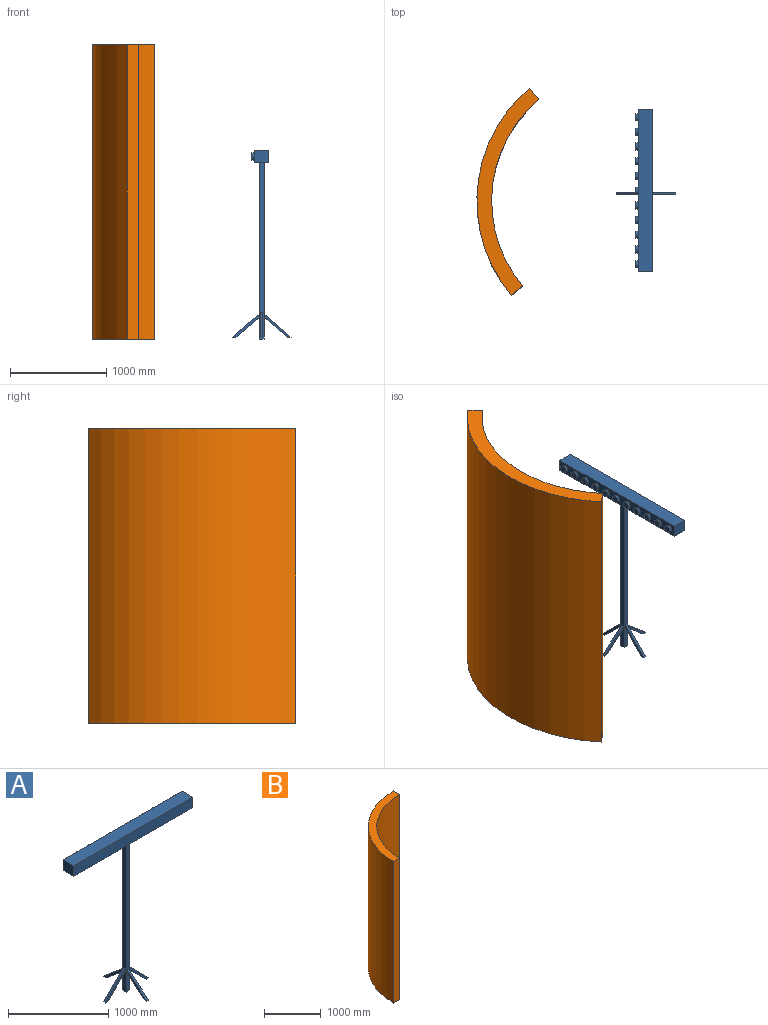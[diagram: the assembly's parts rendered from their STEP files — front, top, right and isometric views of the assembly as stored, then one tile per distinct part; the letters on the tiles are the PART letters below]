
ASSEMBLY  parts=2 mates=1
PART A: 53 faces, bbox 1676.4x609.6x1955.8 mm
  f0: plane 1828.8x50.8mm, normal (1,0,0), area 91990.6mm2, adj f2,f3,f4,f5,f16,f17,f18,f19
  f1: plane 1828.8x50.8mm, normal (-1,0,0), area 91990.6mm2, adj f2,f3,f4,f5,f12,f13,f14,f15
  f2: plane 50.8x50.8mm, normal (0,0,-1), area 2580.6mm2, adj f0,f1,f3,f4
  f3: plane 1828.8x50.8mm, normal (0,-1,0), area 92056.4mm2, adj f0,f1,f2,f5,f26,f28,f29,f30
  f4: plane 1828.8x50.8mm, normal (0,1,0), area 92056.4mm2, adj f0,f1,f2,f5,f22,f23,f24,f25
  f5: plane 1676.4x152.4mm, normal (0,0,-1), area 252902.7mm2, adj f0,f1,f3,f4,f6,f8,f9,f10
  f6: plane 152.4x127mm, normal (1,0,0), area 19354.8mm2, adj f5,f7,f9,f10
  f7: plane 1676.4x152.4mm, normal (0,0,1), area 255483.4mm2, adj f6,f8,f9,f10
  f8: plane 152.4x127mm, normal (-1,0,0), area 19354.8mm2, adj f5,f7,f9,f10
  f9: plane 1676.4x127mm, normal (0,-1,0), area 212902.8mm2, adj f5,f6,f7,f8
  f10: plane 1676.4x127mm, normal (0,1,0), area 162738.8mm2, adj f5,f6,f7,f8,f31,f33,f35,f37
  f11: plane 35.92x25.4mm, normal (0,0,-1), area 912.4mm2, adj f12,f13,f14,f15
  f12: plane 279.4x279.4mm, normal (0,-1,0), area 9391.2mm2, adj f1,f11,f14,f15
  f13: plane 279.4x279.4mm, normal (0,1,0), area 9391.2mm2, adj f1,f11,f14,f15
  f14: plane 243.48x243.48mm, normal (0.71,0,-0.71), area 8746mm2, adj f1,f11,f12,f13
  f15: plane 279.4x279.4mm, normal (-0.71,0,0.71), area 10036.3mm2, adj f1,f11,f12,f13
  f16: plane 243.48x243.48mm, normal (-0.71,0,-0.71), area 8746mm2, adj f0,f18,f19,f20
  f17: plane 279.4x279.4mm, normal (0.71,0,0.71), area 10036.3mm2, adj f0,f18,f19,f20
  f18: plane 279.4x279.4mm, normal (0,-1,0), area 9391.2mm2, adj f0,f16,f17,f20
  f19: plane 279.4x279.4mm, normal (0,1,0), area 9391.2mm2, adj f0,f16,f17,f20
  f20: plane 35.92x25.4mm, normal (0,0,-1), area 912.4mm2, adj f16,f17,f18,f19
  f21: plane 39.22x25.4mm, normal (0,0,-1), area 996.2mm2, adj f22,f23,f24,f25
  f22: plane 279.4x237.46mm, normal (-1,0,0), area 8659.9mm2, adj f4,f21,f24,f25
  f23: plane 279.4x237.46mm, normal (1,0,0), area 8659.9mm2, adj f4,f21,f24,f25
  f24: plane 240.18x204.12mm, normal (0,-0.65,-0.76), area 8006.1mm2, adj f4,f21,f22,f23
  f25: plane 279.4x237.46mm, normal (0,0.65,0.76), area 9313.6mm2, adj f4,f21,f22,f23
  f26: plane 279.4x237.46mm, normal (0,-0.65,0.76), area 9313.6mm2, adj f3,f27,f29,f30
  f27: plane 39.22x25.4mm, normal (0,0,-1), area 996.2mm2, adj f26,f28,f29,f30
  f28: plane 240.18x204.12mm, normal (0,0.65,-0.76), area 8006.1mm2, adj f3,f27,f29,f30
  f29: plane 279.4x237.46mm, normal (1,0,0), area 8659.9mm2, adj f3,f26,f27,f28
  f30: plane 279.4x237.46mm, normal (-1,0,0), area 8659.9mm2, adj f3,f26,f27,f28
  f31: cylinder r=38.1mm len=76.2mm, axis (0,-1,0), area 6080.5mm2, adj f10,f32
  f32: plane 76.2x76.2mm, normal (0,1,0), area 4560.4mm2, adj f31
  f33: cylinder r=38.1mm len=76.2mm, axis (0,-1,0), area 6080.5mm2, adj f10,f34
  f34: plane 76.2x76.2mm, normal (0,1,0), area 4560.4mm2, adj f33
  f35: cylinder r=38.1mm len=76.2mm, axis (0,-1,0), area 6080.5mm2, adj f10,f36
  f36: plane 76.2x76.2mm, normal (0,1,0), area 4560.4mm2, adj f35
  f37: cylinder r=38.1mm len=76.2mm, axis (0,-1,0), area 6080.5mm2, adj f10,f38
  f38: plane 76.2x76.2mm, normal (0,1,0), area 4560.4mm2, adj f37
  f39: cylinder r=38.1mm len=76.2mm, axis (0,-1,0), area 6080.5mm2, adj f10,f40
  f40: plane 76.2x76.2mm, normal (0,1,0), area 4560.4mm2, adj f39
  f41: cylinder r=38.1mm len=76.2mm, axis (0,-1,0), area 6080.5mm2, adj f10,f42
  f42: plane 76.2x76.2mm, normal (0,1,0), area 4560.4mm2, adj f41
  f43: cylinder r=38.1mm len=76.2mm, axis (0,-1,0), area 6080.5mm2, adj f10,f44
  f44: plane 76.2x76.2mm, normal (0,1,0), area 4560.4mm2, adj f43
  f45: cylinder r=38.1mm len=76.2mm, axis (0,-1,0), area 6080.5mm2, adj f10,f46
  f46: plane 76.2x76.2mm, normal (0,1,0), area 4560.4mm2, adj f45
  f47: cylinder r=38.1mm len=76.2mm, axis (0,-1,0), area 6080.5mm2, adj f10,f48
  f48: plane 76.2x76.2mm, normal (0,1,0), area 4560.4mm2, adj f47
  f49: cylinder r=38.1mm len=76.2mm, axis (0,-1,0), area 6080.5mm2, adj f10,f50
  f50: plane 76.2x76.2mm, normal (0,1,0), area 4560.4mm2, adj f49
  f51: cylinder r=38.1mm len=76.2mm, axis (0,-1,0), area 6080.5mm2, adj f10,f52
  f52: plane 76.2x76.2mm, normal (0,1,0), area 4560.4mm2, adj f51
PART B: 6 faces, bbox 1524x1524x3048 mm
  f0: plane 3048x152.4mm, normal (1,0,0), area 464515.2mm2, adj f1,f3,f4,f5
  f1: cylinder r=1524mm len=3048mm, axis (0,0,-1), area 7296587.7mm2, adj f0,f2,f4,f5
  f2: plane 3048x152.4mm, normal (0,-1,0), area 464515.2mm2, adj f1,f3,f4,f5
  f3: cylinder r=1371.6mm len=3048mm, axis (0,0,-1), area 6566928.9mm2, adj f0,f2,f4,f5
  f4: plane 1524x1524mm, normal (0,0,1), area 346587.9mm2, adj f0,f1,f2,f3
  f5: plane 1524x1524mm, normal (0,0,-1), area 346587.9mm2, adj f0,f1,f2,f3
PLACE A rot(axis=(0,0,1),90deg) t=(721.78,-416.56,-345)mm
PLACE B rot(axis=(0,0,1),40deg) t=(497,-497.98,-345)mm
MATE planar B.f5 <-> A.f2  axis (0,0,-1) through (-802.72,-384.27,-345)mm
